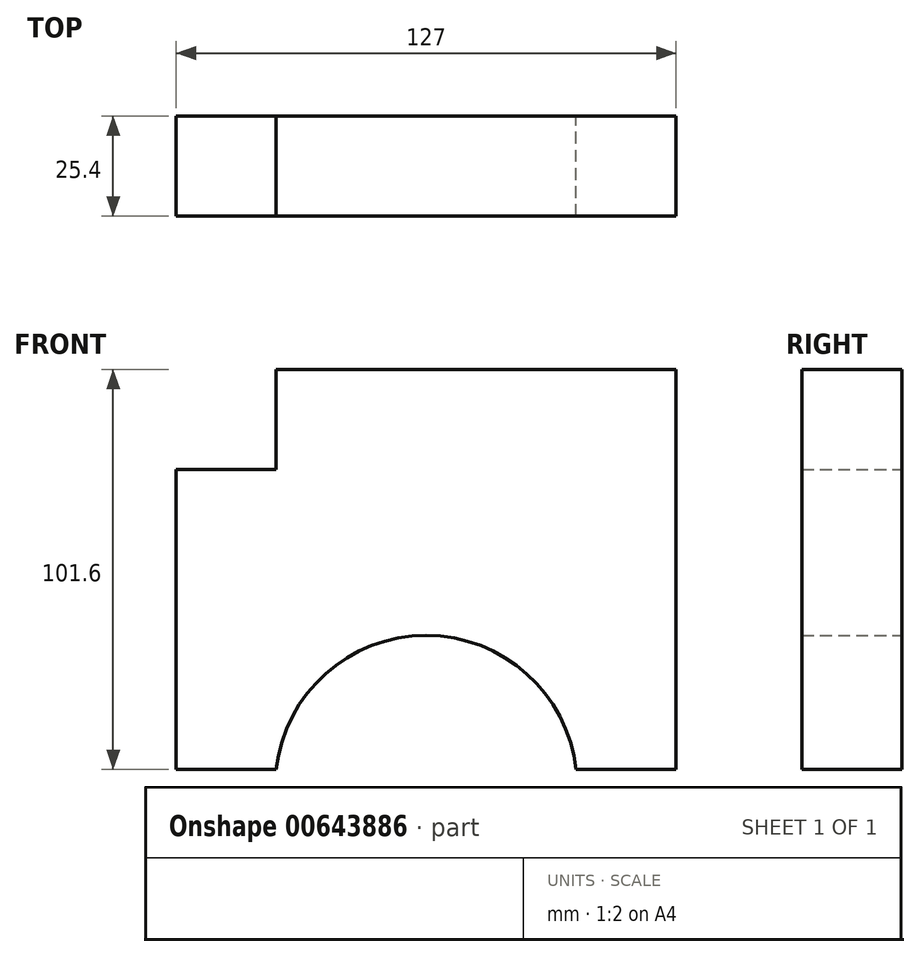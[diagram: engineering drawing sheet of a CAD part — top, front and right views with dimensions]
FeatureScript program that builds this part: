
annotation { "Feature Type Name" : "Feature", "Feature Type Description" : "" }
export const myFeature = defineFeature(function(context is Context, id is Id, definition is map)
    precondition{}
    {
        {
            var Q0;
            Q0=qCreatedBy(makeId("Front.planeOp"),FACE);
            var sketch = newSketch(context, id + "F0", { "sketchPlane" : qUnion([Q0])});
            skLineSegment(sketch, "E0", {"start": v(80.11, 52.15) * mm, "end": v(80.11, -49.45) * mm});
            skLineSegment(sketch, "E1", {"start": v(80.11, -49.45) * mm, "end": v(54.71, -49.45) * mm});
            skLineSegment(sketch, "E2", {"start": v(80.11, 52.15) * mm, "end": v(-21.49, 52.15) * mm});
            skLineSegment(sketch, "E3", {"start": v(-21.49, 52.15) * mm, "end": v(-21.49, 26.75) * mm});
            skLineSegment(sketch, "E4", {"start": v(-21.49, 26.75) * mm, "end": v(-46.89, 26.75) * mm});
            skLineSegment(sketch, "E5", {"start": v(-46.89, 26.75) * mm, "end": v(-46.89, -49.45) * mm});
            skLineSegment(sketch, "E6", {"start": v(-46.89, -49.45) * mm, "end": v(-21.49, -49.45) * mm});
            skArc(sketch, "E7", {"start": v(54.71, -49.45) * mm, "mid": v(16.61, -15.4) * mm, "end": v(-21.49, -49.45) * mm});
            skSolve(sketch);
        }
        {
            var Q0;
            Q0 = qSketchRegion(id + "F0", true);
            extrude(context, id + "F1", {"entities" : qUnion([Q0]), "depth" : 25.4 * mm, "offsetDistance" : 25.4 * mm});
        }
    });
